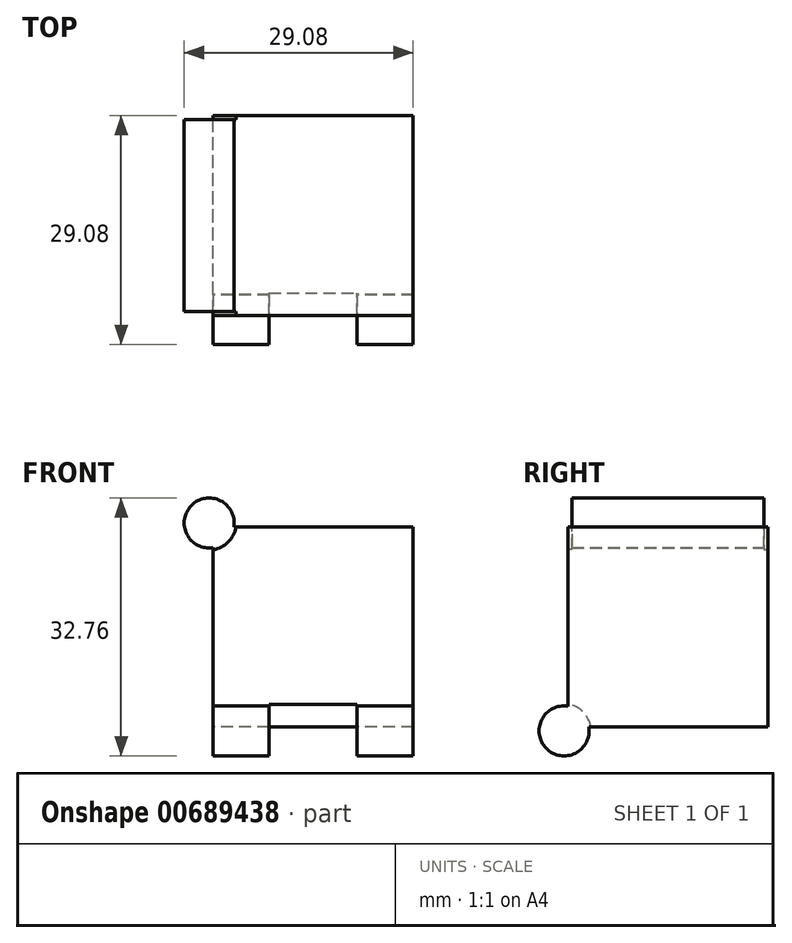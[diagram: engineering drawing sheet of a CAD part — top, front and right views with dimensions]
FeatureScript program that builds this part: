
annotation { "Feature Type Name" : "Feature", "Feature Type Description" : "" }
export const myFeature = defineFeature(function(context is Context, id is Id, definition is map)
    precondition{}
    {
        {
            assignVariable(context, id + "F0", {"name" : "O", "anyValue" : .2});
        }
        {
            var Q0;
            Q0=qCreatedBy(makeId("Front.planeOp"),FACE);
            var sketch = newSketch(context, id + "F1", { "sketchPlane" : qUnion([Q0])});
            skLineSegment(sketch, "E0.bottom", {"start": v(12.7, -12.7) * mm, "end": v(-12.7, -12.7) * mm});
            skLineSegment(sketch, "E0.top", {"start": v(12.7, 12.7) * mm, "end": v(-12.7, 12.7) * mm});
            skLineSegment(sketch, "E0.left", {"start": v(12.7, -12.7) * mm, "end": v(12.7, 12.7) * mm});
            skLineSegment(sketch, "E0.right", {"start": v(-12.7, -12.7) * mm, "end": v(-12.7, 12.7) * mm});
            skPoint(sketch, "E0.middle", {"position": v(0, 0) * mm});
            skSolve(sketch);
        }
        {
            var Q0;
            Q0=makeQuery(id+"F1.imprint","IMPRINT",FACE,{"disambiguationData":[TD([[makeQuery(id+"F1.imprint","IMPRINT",EDGE,{"derivedFrom":sQuery(id+"F1.wireOp",EDGE,"E0.bottom")}),-1.0]])]});
            extrude(context, id + "F2", {"entities" : qUnion([Q0]), "depth" : 25.4 * mm, "offsetDistance" : 25.4 * mm});
        }
        {
            var Q0;
            Q0=makeQuery(id+"F2.opExtrude","SWEPT_FACE",FACE,{"disambiguationData":[OSD([sQuery(id+"F1.wireOp",EDGE,"E0.right")])]});
            var sketch = newSketch(context, id + "F3", { "sketchPlane" : qUnion([Q0])});
            skCircle(sketch, "E1", {"center": v(25.9, -13.2) * mm, "radius": 3.18 * mm});
            skSolve(sketch);
        }
        {
            var Q0;
            {var subQ0=sQuery(id+"F3.wireOp",EDGE,"E1");var subQ1=sQuery(id+"F1.wireOp",EDGE,"E0.right");var subQ4=makeQuery(id+"F2.opExtrude","CAP_EDGE",EDGE,{"disambiguationData":[OSD([subQ1])],"isStart":false});var subQ5=makeQuery(id+"F3.imprint","INTERSECT",VERTEX,{"derivedFrom":[subQ4,subQ0]});Q0=makeQuery(id+"F3.imprint","IMPRINT",FACE,{"disambiguationData":[TD([[makeQuery(id+"F3.imprint","IMPRINT",EDGE,{"disambiguationData":[TD([[subQ5,1.0]])],"derivedFrom":subQ0}),1.0]])]});}
            var Q1;
            Q1=makeQuery(id+"F2.opExtrude","SWEPT_FACE",FACE,{"disambiguationData":[OSD([sQuery(id+"F1.wireOp",EDGE,"E0.left")])]});
            extrude(context, id + "F4", {"entities" : qUnion([Q0]), "operationType" : NewBodyOperationType.ADD, "endBound" : BoundingType.UP_TO_SURFACE, "oppositeDirection" : true, "depth" : 25.4 * mm, "endBoundEntityFace" : qUnion([Q1]), "offsetDistance" : 25.4 * mm});
        }
        {
            var Q0;
            Q0=makeQuery(id+"F2.opExtrude","SWEPT_FACE",FACE,{"disambiguationData":[OSD([sQuery(id+"F1.wireOp",EDGE,"E0.bottom")])]});
            var sketch = newSketch(context, id + "F5", { "sketchPlane" : qUnion([Q0])});
            skLineSegment(sketch, "E2.bottom", {"start": v(5.59, 13.48) * mm, "end": v(-5.59, 13.48) * mm});
            skLineSegment(sketch, "E2.top", {"start": v(5.59, 32.28) * mm, "end": v(-5.59, 32.28) * mm});
            skLineSegment(sketch, "E2.left", {"start": v(5.59, 13.48) * mm, "end": v(5.59, 32.28) * mm});
            skLineSegment(sketch, "E2.right", {"start": v(-5.59, 13.48) * mm, "end": v(-5.59, 32.28) * mm});
            skPoint(sketch, "E2.middle", {"position": v(0, 22.88) * mm});
            skSolve(sketch);
        }
        {
            var Q0;
            {var subQ0=sQuery(id+"F5.wireOp",EDGE,"E2.bottom");Q0=makeQuery(id+"F5.imprint","IMPRINT",FACE,{"disambiguationData":[TD([[makeQuery(id+"F5.imprint","IMPRINT",EDGE,{"derivedFrom":subQ0}),-1.0]])]});}
            var Q1;
            {var subQ0=sQuery(id+"F5.wireOp",EDGE,"E2.top");Q1=makeQuery(id+"F5.imprint","IMPRINT",FACE,{"disambiguationData":[TD([[makeQuery(id+"F5.imprint","IMPRINT",EDGE,{"derivedFrom":subQ0}),1.0]])]});}
            extrude(context, id + "F6", {"entities" : qUnion([Q0, Q1]), "operationType" : NewBodyOperationType.REMOVE, "depth" : 25.4 * mm, "offsetDistance" : 25.4 * mm});
        }
        {
            var Q0;
            Q0=makeQuery(id+"F6.boolean.opBoolean","COPY",FACE,{"derivedFrom":makeQuery(id+"F6.opExtrude","SWEPT_FACE",FACE,{"disambiguationData":[OSD([sQuery(id+"F5.wireOp",EDGE,"E2.left")])]})});
            var sketch = newSketch(context, id + "F7", { "sketchPlane" : qUnion([Q0])});
            skCircle(sketch, "E3", {"center": v(25.9, -13.2) * mm, "radius": 3.43 * mm});
            skSolve(sketch);
        }
        {
            var Q0;
            Q0=makeQuery(id+"F7.imprint","IMPRINT",FACE,{"disambiguationData":[TD([[makeQuery(id+"F7.imprint","IMPRINT",EDGE,{"derivedFrom":sQuery(id+"F7.wireOp",EDGE,"E3")}),1.0]])]});
            var Q1;
            Q1=makeQuery(id+"F6.boolean.opBoolean","COPY",FACE,{"derivedFrom":makeQuery(id+"F6.opExtrude","SWEPT_FACE",FACE,{"disambiguationData":[OSD([sQuery(id+"F5.wireOp",EDGE,"E2.right")])]})});
            extrude(context, id + "F8", {"entities" : qUnion([Q0]), "operationType" : NewBodyOperationType.REMOVE, "endBound" : BoundingType.UP_TO_SURFACE, "depth" : 25.4 * mm, "endBoundEntityFace" : qUnion([Q1]), "offsetDistance" : 25.4 * mm});
        }
        {
            var Q0;
            Q0=makeQuery(id+"F2.opExtrude","CAP_FACE",FACE,{"disambiguationData":[OSD([sQuery(id+"F1.wireOp",EDGE,"E0.bottom"),sQuery(id+"F1.wireOp",EDGE,"E0.top"),sQuery(id+"F1.wireOp",EDGE,"E0.left"),sQuery(id+"F1.wireOp",EDGE,"E0.right")])],"isStart":true});
            var sketch = newSketch(context, id + "F9", { "sketchPlane" : qUnion([Q0])});
            skCircle(sketch, "E4", {"center": v(13.2, 13.2) * mm, "radius": 3.18 * mm});
            skSolve(sketch);
        }
        {
            var Q0;
            {var subQ0=sQuery(id+"F9.wireOp",EDGE,"E4");var subQ1=makeQuery(id+"F2.opExtrude","CAP_EDGE",EDGE,{"disambiguationData":[OSD([sQuery(id+"F1.wireOp",EDGE,"E0.top")])],"isStart":true});var subQ2=makeQuery(id+"F9.imprint","INTERSECT",VERTEX,{"derivedFrom":[subQ1,subQ0]});Q0=makeQuery(id+"F9.imprint","IMPRINT",FACE,{"disambiguationData":[TD([[makeQuery(id+"F9.imprint","IMPRINT",EDGE,{"disambiguationData":[TD([[subQ2,1.0]])],"derivedFrom":subQ0}),1.0]])]});}
            var Q1;
            Q1=makeQuery(id+"F2.opExtrude","CAP_FACE",FACE,{"disambiguationData":[OSD([sQuery(id+"F1.wireOp",EDGE,"E0.bottom"),sQuery(id+"F1.wireOp",EDGE,"E0.top"),sQuery(id+"F1.wireOp",EDGE,"E0.left"),sQuery(id+"F1.wireOp",EDGE,"E0.right")])],"isStart":false});
            extrude(context, id + "F10", {"entities" : qUnion([Q0]), "operationType" : NewBodyOperationType.ADD, "endBound" : BoundingType.UP_TO_SURFACE, "oppositeDirection" : true, "depth" : 25.4 * mm, "endBoundEntityFace" : qUnion([Q1]), "offsetDistance" : 25.4 * mm});
        }
        {
            var Q0;
            {var subQ0=sQuery(id+"F1.wireOp",EDGE,"E0.right");var subQ1=sQuery(id+"F1.wireOp",EDGE,"E0.left");var subQ2=sQuery(id+"F1.wireOp",EDGE,"E0.top");var subQ3=sQuery(id+"F1.wireOp",EDGE,"E0.bottom");Q0=makeQuery(id+"F10.boolean.opBoolean","MERGE",FACE,{"derivedFrom":[makeQuery(id+"F2.opExtrude","CAP_FACE",FACE,{"disambiguationData":[OSD([subQ3,subQ2,subQ1,subQ0])],"isStart":false}),makeQuery(id+"F10.opExtrude","CAP_FACE",FACE,{"disambiguationData":[OSD([subQ3,subQ2,subQ1,subQ0])],"isStart":false})]});}
            var sketch = newSketch(context, id + "F11", { "sketchPlane" : qUnion([Q0])});
            skCircle(sketch, "E5", {"center": v(-13.2, 13.2) * mm, "radius": 3.43 * mm});
            skSolve(sketch);
        }
        {
            var Q0;
            {var subQ0=sQuery(id+"F1.wireOp",EDGE,"E0.right");var subQ1=sQuery(id+"F1.wireOp",EDGE,"E0.top");Q0=makeQuery(id+"F10.boolean.opBoolean","MERGE",FACE,{"derivedFrom":[makeQuery(id+"F2.opExtrude","CAP_FACE",FACE,{"disambiguationData":[OSD([sQuery(id+"F1.wireOp",EDGE,"E0.bottom"),subQ1,sQuery(id+"F1.wireOp",EDGE,"E0.left"),subQ0])],"isStart":true}),makeQuery(id+"F10.opExtrude","CAP_FACE",FACE,{"disambiguationData":[OSD([subQ1,subQ0,sQuery(id+"F9.wireOp",EDGE,"E4")])],"isStart":true})]});}
            var sketch = newSketch(context, id + "F12", { "sketchPlane" : qUnion([Q0])});
            skCircle(sketch, "E6", {"center": v(13.2, 13.2) * mm, "radius": 3.43 * mm});
            skSolve(sketch);
        }
        {
            var Q0;
            {var subQ5=makeQuery(id+"F10.opExtrude","CAP_EDGE",EDGE,{"disambiguationData":[OSD([sQuery(id+"F9.wireOp",EDGE,"E4")])],"isStart":true});Q0=makeQuery(id+"F12.imprint","IMPRINT",FACE,{"disambiguationData":[TD([[makeQuery(id+"F12.imprint","IMPRINT",EDGE,{"derivedFrom":subQ5}),-1.0]])]});}
            var Q1;
            {var subQ5=makeQuery(id+"F10.opExtrude","CAP_EDGE",EDGE,{"disambiguationData":[OSD([sQuery(id+"F9.wireOp",EDGE,"E4")])],"isStart":true});Q1=makeQuery(id+"F12.imprint","IMPRINT",FACE,{"disambiguationData":[TD([[makeQuery(id+"F12.imprint","IMPRINT",EDGE,{"derivedFrom":subQ5}),1.0]])]});}
            extrude(context, id + "F13", {"entities" : qUnion([Q0, Q1]), "operationType" : NewBodyOperationType.REMOVE, "oppositeDirection" : true, "depth" : (.3 + getVariable(context, 'O')) * mm, "offsetDistance" : 25.4 * mm});
        }
        {
            var Q0;
            {var subQ0=sQuery(id+"F11.wireOp",EDGE,"E5");var subQ1=sQuery(id+"F1.wireOp",EDGE,"E0.top");var subQ2=makeQuery(id+"F2.opExtrude","CAP_EDGE",EDGE,{"disambiguationData":[OSD([subQ1])],"isStart":false});var subQ3=makeQuery(id+"F11.imprint","INTERSECT",VERTEX,{"derivedFrom":[subQ2,subQ0]});Q0=makeQuery(id+"F11.imprint","IMPRINT",FACE,{"disambiguationData":[TD([[makeQuery(id+"F11.imprint","IMPRINT",EDGE,{"disambiguationData":[TD([[subQ3,-1.0]])],"derivedFrom":subQ0}),1.0]])]});}
            var Q1;
            {var subQ0=sQuery(id+"F11.wireOp",EDGE,"E5");var subQ1=sQuery(id+"F1.wireOp",EDGE,"E0.top");var subQ2=makeQuery(id+"F2.opExtrude","CAP_EDGE",EDGE,{"disambiguationData":[OSD([subQ1])],"isStart":false});var subQ3=makeQuery(id+"F11.imprint","INTERSECT",VERTEX,{"derivedFrom":[subQ2,subQ0]});Q1=makeQuery(id+"F11.imprint","IMPRINT",FACE,{"disambiguationData":[TD([[makeQuery(id+"F11.imprint","IMPRINT",EDGE,{"disambiguationData":[TD([[subQ3,1.0]])],"derivedFrom":subQ0}),1.0]])]});}
            extrude(context, id + "F14", {"entities" : qUnion([Q0, Q1]), "operationType" : NewBodyOperationType.REMOVE, "oppositeDirection" : true, "depth" : (.3 + getVariable(context, 'O')) * mm, "offsetDistance" : 25.4 * mm});
        }
    });
